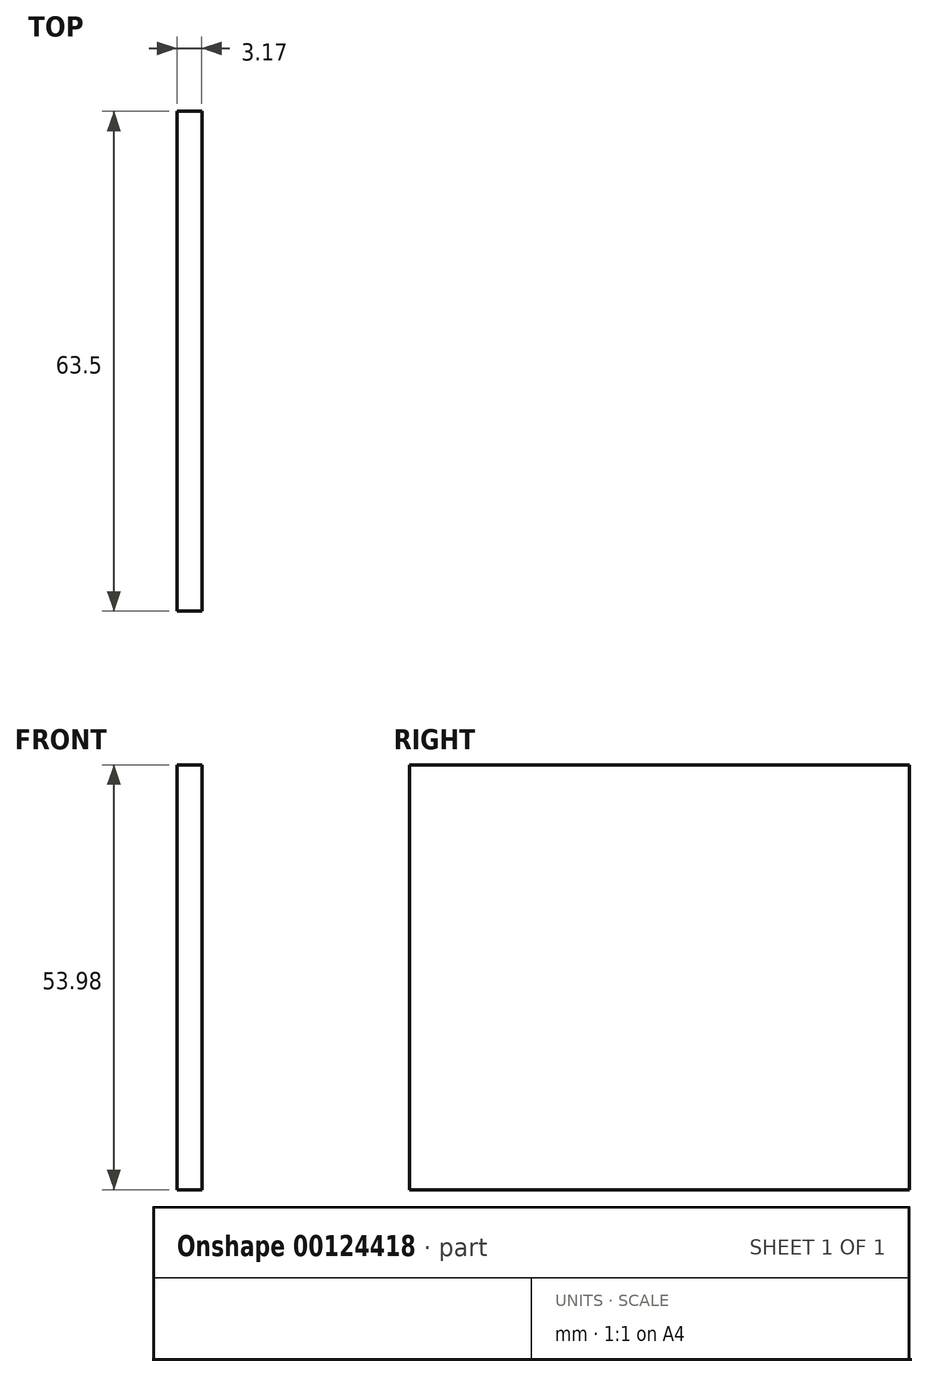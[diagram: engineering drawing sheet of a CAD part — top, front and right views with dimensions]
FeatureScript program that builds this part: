
annotation { "Feature Type Name" : "Feature", "Feature Type Description" : "" }
export const myFeature = defineFeature(function(context is Context, id is Id, definition is map)
    precondition{}
    {
        {
            var Q0;
            Q0=qCreatedBy(makeId("Right.planeOp"),FACE);
            var sketch = newSketch(context, id + "F0", { "sketchPlane" : qUnion([Q0])});
            skLineSegment(sketch, "E0.bottom", {"start": v(31.75, -26.99) * mm, "end": v(-31.75, -26.99) * mm});
            skLineSegment(sketch, "E0.top", {"start": v(31.75, 26.99) * mm, "end": v(-31.75, 26.99) * mm});
            skLineSegment(sketch, "E0.left", {"start": v(31.75, -26.99) * mm, "end": v(31.75, 26.99) * mm});
            skLineSegment(sketch, "E0.right", {"start": v(-31.75, -26.99) * mm, "end": v(-31.75, 26.99) * mm});
            skPoint(sketch, "E0.middle", {"position": v(0, 0) * mm});
            skSolve(sketch);
        }
        {
            var Q0;
            Q0 = qSketchRegion(id + "F0", true);
            extrude(context, id + "F1", {"entities" : qUnion([Q0]), "depth" : 3.17 * mm});
        }
    });
